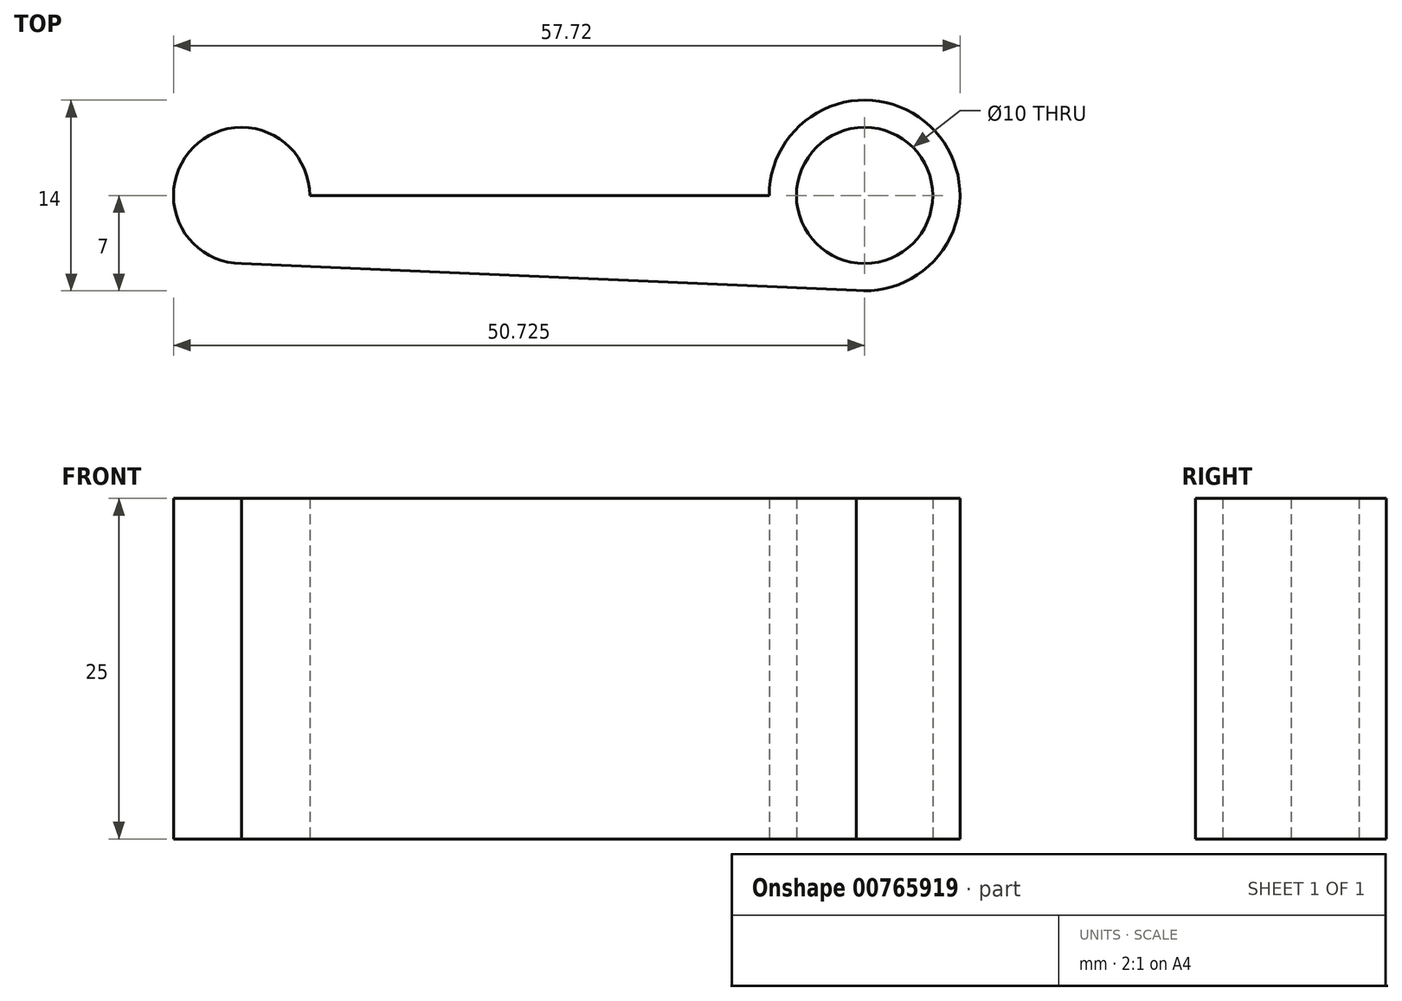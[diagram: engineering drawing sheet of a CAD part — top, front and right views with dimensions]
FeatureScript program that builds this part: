
annotation { "Feature Type Name" : "Feature", "Feature Type Description" : "" }
export const myFeature = defineFeature(function(context is Context, id is Id, definition is map)
    precondition{}
    {
        {
            var Q0;
            Q0=qCreatedBy(makeId("Top.planeOp"),FACE);
            var sketch = newSketch(context, id + "F0", { "sketchPlane" : qUnion([Q0])});
            skCircle(sketch, "E0", {"center": v(0, 0) * mm, "radius": 5 * mm});
            skLineSegment(sketch, "E1", {"start": v(0, 0) * mm, "end": v(22.86, 0) * mm});
            skLineSegment(sketch, "E2", {"start": v(22.86, 0) * mm, "end": v(22.86, 11.49) * mm});
            skCircle(sketch, "E3.MirrorC", {"center": v(45.72, 0) * mm, "radius": 5 * mm});
            skLineSegment(sketch, "E4.MirrorCS", {"start": v(45.72, 0) * mm, "end": v(22.86, 0) * mm});
            skCircle(sketch, "E5", {"center": v(45.72, 0) * mm, "radius": 7 * mm});
            skLineSegment(sketch, "E6", {"start": v(45.72, 0) * mm, "end": v(45.72, -7) * mm});
            skLineSegment(sketch, "E7", {"start": v(45.72, -7) * mm, "end": v(45.72, -7) * mm});
            skLineSegment(sketch, "E8", {"start": v(45.72, -7) * mm, "end": v(0, -5) * mm});
            skSolve(sketch);
        }
        {
            var Q0;
            {var subQ0=sQuery(id+"F0.wireOp",EDGE,"E5");var subQ1=sQuery(id+"F0.wireOp",EDGE,"E4.MirrorCS");var subQ2=makeQuery(id+"F0.imprint","INTERSECT",VERTEX,{"derivedFrom":[subQ1,subQ0]});Q0=makeQuery(id+"F0.imprint","IMPRINT",FACE,{"disambiguationData":[TD([[makeQuery(id+"F0.imprint","IMPRINT",EDGE,{"disambiguationData":[TD([[subQ2,1.0]])],"derivedFrom":subQ1}),-1.0]])]});}
            var Q1;
            Q1 = qSketchRegion(id + "F0", true);
            var Q2;
            {var subQ3=sQuery(id+"F0.wireOp",EDGE,"E8");var subQ7=sQuery(id+"F0.wireOp",EDGE,"E0");var subQ9=makeQuery(id+"F0.imprint","INTERSECT",VERTEX,{"derivedFrom":[subQ7,subQ3]});Q2=makeQuery(id+"F0.imprint","IMPRINT",FACE,{"disambiguationData":[TD([[makeQuery(id+"F0.imprint","IMPRINT",EDGE,{"disambiguationData":[TD([[subQ9,-1.0]])],"derivedFrom":subQ7}),-1.0]])]});}
            extrude(context, id + "F1", {"entities" : qUnion([Q0, Q1, Q2]), "depth" : 25 * mm, "offsetDistance" : 25 * mm});
        }
    });
